# Revit family: Smoke-Detector
name_source: partatom
category: Electrical Fixtures
units: mm (PartAtom-declared; Revit-internal decimal feet)

## family parameters
Always vertical = Yes
Classification Number = 23.85.30.21.11.11.11
Cut with Voids When Loaded = No
Host = Ceiling
Maintain Annotation Orientation = No
Part Type = Normal
Room Calculation Point = No
Round Connector Dimension = Use Diameter
Shared = No

## types (1)
- Smoke-Detector
    Alarm Volume (dB) = 80
    Assembly Code = D4030
    Battery Type = 9V
    Case Material = ARCAT - Plastic, ABS - White
    Construction Details = http://www.arcat.com
    Cost = 0 $
    Default Elevation = 0' - 0"
    Depth = 0' - 1 1/2"
    Description = Hard Wired Smoke Alarm
    Diameter = 0' - 5"
    Expected Lifespan (Years) = 10
    Green Building-LEED = http://www.arcat.com
    Keynote = 13850
    Maintenance Schedule (Months) = 6
    Manufacturer = Generic
    Manufacturer Fax = (203) 929-2444
    Manufacturer Website = http://www.arcat.com
    Model = Generic
    Product Data = http://www.arcat.com
    Product Properties = http://www.arcat.com
    Specification = http://www.arcat.com
    UL 218 Compliant = Yes
    URL = http://www.arcat.com
    Voltage = 120
    Warranty Duration (Years) = 10

## geometry (parser evidence)
native form markers: Sweep x5
no freeform markers — native parametric forms only
